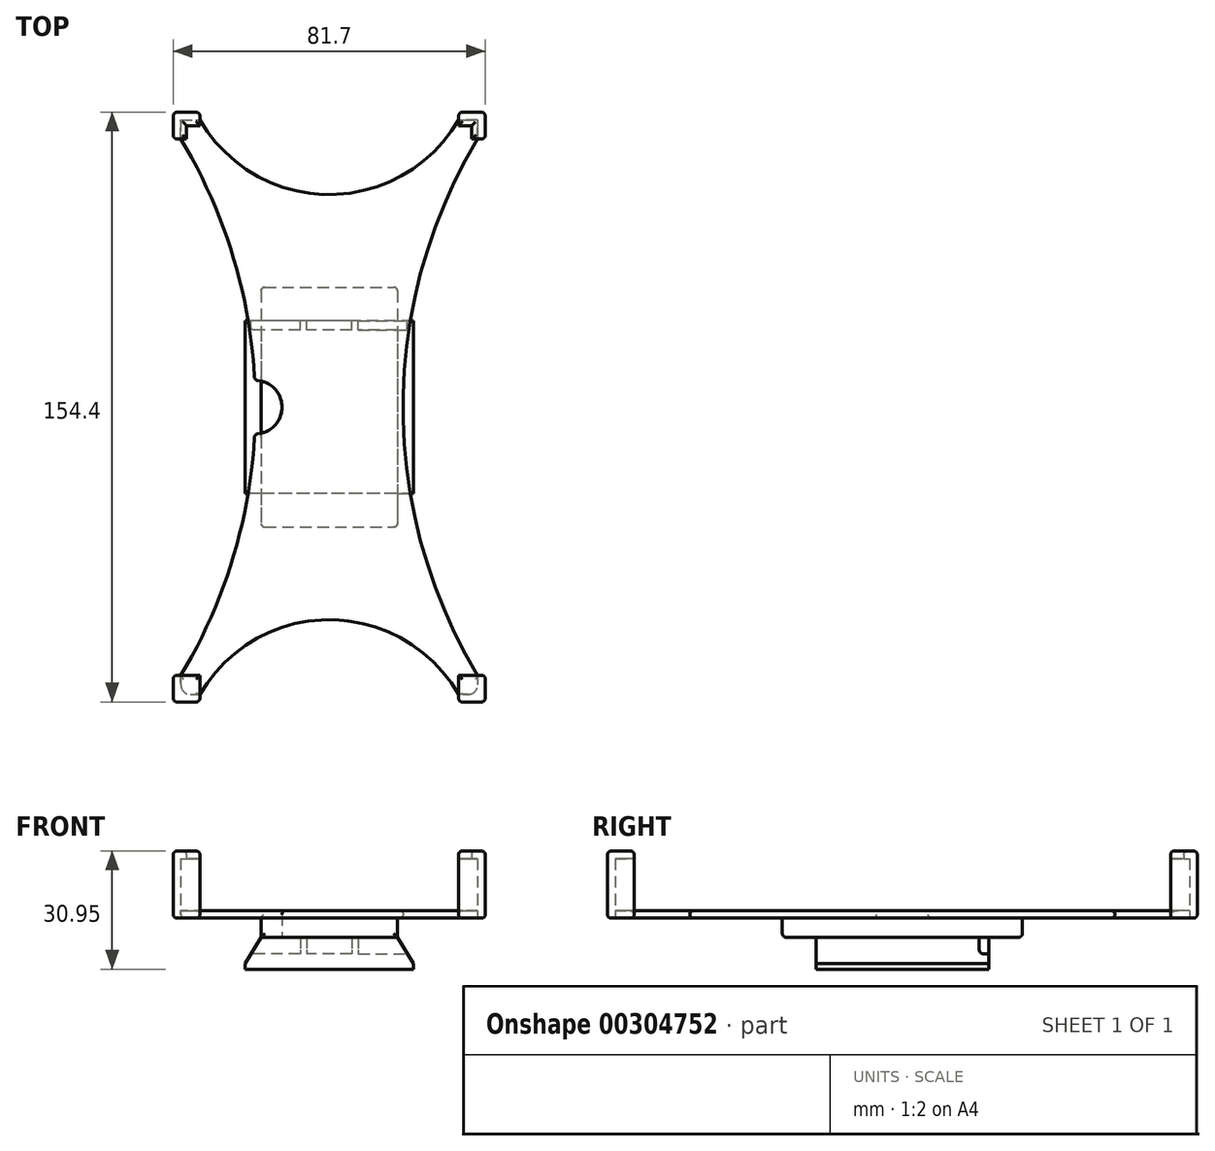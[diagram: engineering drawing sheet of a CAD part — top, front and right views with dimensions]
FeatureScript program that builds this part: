
annotation { "Feature Type Name" : "Feature", "Feature Type Description" : "" }
export const myFeature = defineFeature(function(context is Context, id is Id, definition is map)
    precondition{}
    {
        {
            var Q0;
            Q0=qCreatedBy(makeId("Top.planeOp"),FACE);
            var sketch = newSketch(context, id + "F0", { "sketchPlane" : qUnion([Q0])});
            skLineSegment(sketch, "E0.bottom", {"start": v(-38.85, 75.2) * mm, "end": v(-33.85, 75.2) * mm});
            skLineSegment(sketch, "E0.top", {"start": v(-38.85, -75.2) * mm, "end": v(-33.85, -75.2) * mm});
            skLineSegment(sketch, "E0.left", {"start": v(-38.85, 75.2) * mm, "end": v(-38.85, 70.2) * mm});
            skLineSegment(sketch, "E0.right", {"start": v(38.85, 75.2) * mm, "end": v(38.85, 70.2) * mm});
            skLineSegment(sketch, "E1", {"start": v(-38.85, 75.2) * mm, "end": v(38.85, -75.2) * mm, "construction": true});
            skArc(sketch, "E2", {"start": v(-33.85, 75.2) * mm, "mid": v(0, 55.65) * mm, "end": v(33.85, 75.2) * mm});
            skArc(sketch, "E3", {"start": v(-38.85, -70.2) * mm, "mid": v(-25.3, -39.79) * mm, "end": v(-19.53, -7) * mm});
            skArc(sketch, "E4.MirrorCS", {"start": v(38.85, -70.2) * mm, "mid": v(19.35, 0) * mm, "end": v(38.85, 70.2) * mm});
            skArc(sketch, "E5.MirrorCS", {"start": v(-33.85, -75.2) * mm, "mid": v(0, -55.65) * mm, "end": v(33.85, -75.2) * mm});
            skArc(sketch, "E6", {"start": v(-19.53, -7) * mm, "mid": v(-12.35, 0) * mm, "end": v(-19.53, 7) * mm});
            skArc(sketch, "E7.trimOffspring", {"start": v(-19.53, 7) * mm, "mid": v(-25.3, 39.79) * mm, "end": v(-38.85, 70.2) * mm});
            skLineSegment(sketch, "E8.bottom", {"start": v(-25.25, 66.5) * mm, "end": v(25.25, 66.5) * mm, "construction": true});
            skLineSegment(sketch, "E8.top", {"start": v(-25.25, 64.9) * mm, "end": v(25.25, 64.9) * mm, "construction": true});
            skLineSegment(sketch, "E8.left", {"start": v(-25.25, 66.5) * mm, "end": v(-25.25, 64.9) * mm, "construction": true});
            skLineSegment(sketch, "E8.right", {"start": v(25.25, 66.5) * mm, "end": v(25.25, 64.9) * mm, "construction": true});
            skLineSegment(sketch, "E9.trimOffspring", {"start": v(33.85, 75.2) * mm, "end": v(38.85, 75.2) * mm});
            skLineSegment(sketch, "E10.trimOffspring", {"start": v(-38.85, -70.2) * mm, "end": v(-38.85, -75.2) * mm});
            skLineSegment(sketch, "E11.trimOffspring", {"start": v(38.85, -70.2) * mm, "end": v(38.85, -75.2) * mm});
            skLineSegment(sketch, "E12.trimOffspring", {"start": v(33.85, -75.2) * mm, "end": v(38.85, -75.2) * mm});
            skSolve(sketch);
        }
        {
            var Q0;
            Q0=qSketchRegion(id+"F0",true);
            extrude(context, id + "F1", {"entities" : qUnion([Q0]), "depth" : 2 * mm});
        }
        {
            var Q0;
            Q0=qCreatedBy(makeId("Top.planeOp"),FACE);
            var sketch = newSketch(context, id + "F2", { "sketchPlane" : qUnion([Q0])});
            skLineSegment(sketch, "E13", {"start": v(-33.85, 75.2) * mm, "end": v(-33.85, 77.2) * mm});
            skLineSegment(sketch, "E14", {"start": v(-33.85, 77.2) * mm, "end": v(-40.85, 77.2) * mm});
            skLineSegment(sketch, "E15", {"start": v(-40.85, 77.2) * mm, "end": v(-40.85, 70.2) * mm});
            skLineSegment(sketch, "E16", {"start": v(-40.85, 70.2) * mm, "end": v(-38.85, 70.2) * mm});
            skLineSegment(sketch, "E17", {"start": v(-38.85, 70.2) * mm, "end": v(-38.85, 75.2) * mm});
            skLineSegment(sketch, "E18", {"start": v(-38.85, 75.2) * mm, "end": v(-33.85, 75.2) * mm});
            skLineSegment(sketch, "E19.MirrorCS", {"start": v(40.85, 77.2) * mm, "end": v(40.85, 70.2) * mm});
            skLineSegment(sketch, "E20.MirrorCS", {"start": v(33.85, 77.2) * mm, "end": v(40.85, 77.2) * mm});
            skLineSegment(sketch, "E21.MirrorCS", {"start": v(40.85, 70.2) * mm, "end": v(38.85, 70.2) * mm});
            skLineSegment(sketch, "E22.MirrorCS", {"start": v(38.85, 75.2) * mm, "end": v(33.85, 75.2) * mm});
            skLineSegment(sketch, "E23.MirrorCS", {"start": v(38.85, 70.2) * mm, "end": v(38.85, 75.2) * mm});
            skLineSegment(sketch, "E24.MirrorCS", {"start": v(33.85, 75.2) * mm, "end": v(33.85, 77.2) * mm});
            skLineSegment(sketch, "E25.MirrorCS", {"start": v(33.85, -75.2) * mm, "end": v(33.85, -77.2) * mm});
            skLineSegment(sketch, "E26.MirrorCS", {"start": v(40.85, -70.2) * mm, "end": v(38.85, -70.2) * mm});
            skLineSegment(sketch, "E27.MirrorCS", {"start": v(-33.85, -75.2) * mm, "end": v(-33.85, -77.2) * mm});
            skLineSegment(sketch, "E28.MirrorCS", {"start": v(-40.85, -70.2) * mm, "end": v(-38.85, -70.2) * mm});
            skLineSegment(sketch, "E29.MirrorCS", {"start": v(38.85, -70.2) * mm, "end": v(38.85, -75.2) * mm});
            skLineSegment(sketch, "E30.MirrorCS", {"start": v(38.85, -75.2) * mm, "end": v(33.85, -75.2) * mm});
            skLineSegment(sketch, "E31.MirrorCS", {"start": v(33.85, -77.2) * mm, "end": v(40.85, -77.2) * mm});
            skLineSegment(sketch, "E32.MirrorCS", {"start": v(40.85, -77.2) * mm, "end": v(40.85, -70.2) * mm});
            skLineSegment(sketch, "E33.MirrorCS", {"start": v(-38.85, -75.2) * mm, "end": v(-33.85, -75.2) * mm});
            skLineSegment(sketch, "E34.MirrorCS", {"start": v(-38.85, -70.2) * mm, "end": v(-38.85, -75.2) * mm});
            skLineSegment(sketch, "E35.MirrorCS", {"start": v(-33.85, -77.2) * mm, "end": v(-40.85, -77.2) * mm});
            skLineSegment(sketch, "E36.MirrorCS", {"start": v(-40.85, -77.2) * mm, "end": v(-40.85, -70.2) * mm});
            skSolve(sketch);
        }
        {
            var Q0;
            Q0=qSketchRegion(id+"F2",true);
            extrude(context, id + "F3", {"entities" : qUnion([Q0]), "operationType" : NewBodyOperationType.ADD, "depth" : (13.6 + 2) * mm});
        }
        {
            var Q0;
            Q0=makeQuery(id+"F3.opExtrude","CAP_FACE",FACE,{"disambiguationData":[OSD([sQuery(id+"F2.wireOp",EDGE,"E13"),sQuery(id+"F2.wireOp",EDGE,"E14"),sQuery(id+"F2.wireOp",EDGE,"E15"),sQuery(id+"F2.wireOp",EDGE,"E16"),sQuery(id+"F2.wireOp",EDGE,"E17"),sQuery(id+"F2.wireOp",EDGE,"E18")])],"isStart":false});
            var sketch = newSketch(context, id + "F4", { "sketchPlane" : qUnion([Q0])});
            skLineSegment(sketch, "E37.bottom", {"start": v(-40.85, -77.2) * mm, "end": v(-33.85, -77.2) * mm});
            skLineSegment(sketch, "E37.top", {"start": v(-40.85, -70.2) * mm, "end": v(-33.85, -70.2) * mm});
            skLineSegment(sketch, "E37.left", {"start": v(-40.85, -77.2) * mm, "end": v(-40.85, -70.2) * mm});
            skLineSegment(sketch, "E37.right", {"start": v(-33.85, -77.2) * mm, "end": v(-33.85, -70.2) * mm});
            skLineSegment(sketch, "E38", {"start": v(-40.85, 77.2) * mm, "end": v(-33.85, 77.2) * mm});
            skLineSegment(sketch, "E39", {"start": v(-33.85, 77.2) * mm, "end": v(-33.85, 73.7) * mm});
            skLineSegment(sketch, "E40", {"start": v(-33.85, 73.7) * mm, "end": v(-37.35, 73.7) * mm});
            skLineSegment(sketch, "E41", {"start": v(-37.35, 73.7) * mm, "end": v(-37.35, 70.2) * mm});
            skLineSegment(sketch, "E42", {"start": v(-37.35, 70.2) * mm, "end": v(-40.85, 70.2) * mm});
            skLineSegment(sketch, "E43", {"start": v(-40.85, 70.2) * mm, "end": v(-40.85, 77.2) * mm});
            skLineSegment(sketch, "E44.MirrorCS", {"start": v(33.85, 77.2) * mm, "end": v(33.85, 73.7) * mm});
            skLineSegment(sketch, "E45.MirrorCS", {"start": v(37.35, 70.2) * mm, "end": v(40.85, 70.2) * mm});
            skLineSegment(sketch, "E46.MirrorCS", {"start": v(33.85, 73.7) * mm, "end": v(37.35, 73.7) * mm});
            skLineSegment(sketch, "E47.MirrorCS", {"start": v(37.35, 73.7) * mm, "end": v(37.35, 70.2) * mm});
            skLineSegment(sketch, "E48.MirrorCS", {"start": v(40.85, -77.2) * mm, "end": v(40.85, -70.2) * mm});
            skLineSegment(sketch, "E49.MirrorCS", {"start": v(40.85, -70.2) * mm, "end": v(33.85, -70.2) * mm});
            skLineSegment(sketch, "E50.MirrorCS", {"start": v(40.85, 70.2) * mm, "end": v(40.85, 77.2) * mm});
            skLineSegment(sketch, "E51.MirrorCS", {"start": v(40.85, -77.2) * mm, "end": v(33.85, -77.2) * mm});
            skLineSegment(sketch, "E52.MirrorCS", {"start": v(40.85, 77.2) * mm, "end": v(33.85, 77.2) * mm});
            skLineSegment(sketch, "E53.MirrorCS", {"start": v(33.85, -77.2) * mm, "end": v(33.85, -70.2) * mm});
            skSolve(sketch);
        }
        {
            var Q0;
            Q0=qSketchRegion(id+"F4",true);
            extrude(context, id + "F5", {"entities" : qUnion([Q0]), "operationType" : NewBodyOperationType.ADD, "depth" : 2 * mm});
        }
        {
            var Q0;
            Q0=qCreatedBy(makeId("Top.planeOp"),FACE);
            var sketch = newSketch(context, id + "F6", { "sketchPlane" : qUnion([Q0])});
            skLineSegment(sketch, "E54.bottom", {"start": v(-17.85, 31.43) * mm, "end": v(17.85, 31.43) * mm});
            skLineSegment(sketch, "E54.top", {"start": v(-17.85, -31.42) * mm, "end": v(17.85, -31.42) * mm});
            skLineSegment(sketch, "E54.left", {"start": v(-17.85, 31.43) * mm, "end": v(-17.85, 6.84) * mm});
            skLineSegment(sketch, "E54.right", {"start": v(17.85, 31.43) * mm, "end": v(17.85, -31.42) * mm});
            skLineSegment(sketch, "E55", {"start": v(-17.85, 31.43) * mm, "end": v(17.85, -31.43) * mm, "construction": true});
            skArc(sketch, "E56", {"start": v(-17.85, -6.84) * mm, "mid": v(-12.35, 0) * mm, "end": v(-17.85, 6.84) * mm});
            skLineSegment(sketch, "E57.trimOffspring", {"start": v(-17.85, -6.84) * mm, "end": v(-17.85, -31.42) * mm});
            skSolve(sketch);
        }
        {
            var Q0;
            Q0=qSketchRegion(id+"F6",true);
            extrude(context, id + "F7", {"entities" : qUnion([Q0]), "operationType" : NewBodyOperationType.ADD, "oppositeDirection" : true, "depth" : 5 * mm});
        }
        {
            var Q0;
            Q0=makeQuery(id+"F7.opExtrude","CAP_FACE",FACE,{"disambiguationData":[OSD([sQuery(id+"F6.wireOp",EDGE,"E54.bottom"),sQuery(id+"F6.wireOp",EDGE,"E54.top"),sQuery(id+"F6.wireOp",EDGE,"E54.left"),sQuery(id+"F6.wireOp",EDGE,"E54.right"),sQuery(id+"F6.wireOp",EDGE,"E56"),sQuery(id+"F6.wireOp",EDGE,"E57.trimOffspring")])],"isStart":false});
            var sketch = newSketch(context, id + "F8", { "sketchPlane" : qUnion([Q0])});
            skLineSegment(sketch, "E58.bottom", {"start": v(17.85, -22.62) * mm, "end": v(-17.85, -22.62) * mm});
            skLineSegment(sketch, "E58.top", {"start": v(17.85, 22.62) * mm, "end": v(-17.85, 22.62) * mm});
            skLineSegment(sketch, "E58.left", {"start": v(17.85, -22.62) * mm, "end": v(17.85, 22.62) * mm});
            skLineSegment(sketch, "E58.right", {"start": v(-17.85, -22.62) * mm, "end": v(-17.85, 22.62) * mm});
            skPoint(sketch, "E58.middle", {"position": v(0, 0) * mm});
            skSolve(sketch);
        }
        {
            var Q0;
            {var subQ2=sQuery(id+"F8.wireOp",EDGE,"E58.bottom");Q0=makeQuery(id+"F8.imprint","IMPRINT",FACE,{"disambiguationData":[TD([[makeQuery(id+"F8.imprint","IMPRINT",EDGE,{"derivedFrom":subQ2}),-1.0]])]});}
            cPlane(context, id + "F9", {"entities" : qUnion([Q0]), "cplaneType" : CPlaneType.OFFSET, "offset" : 6.85 * mm, "width" : 150 * mm, "height" : 150 * mm});
        }
        {
            var Q0;
            Q0=qCreatedBy(id+"F9.planeOp",FACE);
            var sketch = newSketch(context, id + "F10", { "sketchPlane" : qUnion([Q0])});
            skLineSegment(sketch, "E59.bottom", {"start": v(22, -22.62) * mm, "end": v(-22, -22.62) * mm});
            skLineSegment(sketch, "E59.top", {"start": v(22, 22.62) * mm, "end": v(-22, 22.62) * mm});
            skLineSegment(sketch, "E59.left", {"start": v(22, -22.62) * mm, "end": v(22, 22.62) * mm});
            skLineSegment(sketch, "E59.right", {"start": v(-22, -22.62) * mm, "end": v(-22, 22.62) * mm});
            skPoint(sketch, "E59.middle", {"position": v(0, 0) * mm});
            skSolve(sketch);
        }
        {
            var Q1;
            Q1=qSketchRegion(id+"F8",true);
            var Q2;
            Q2=qSketchRegion(id+"F10",true);
            var Q3;
            Q3=sQuery(id+"F8.wireOp",VERTEX,"E58.right.end");
            var Q4;
            Q4=sQuery(id+"F10.wireOp",VERTEX,"E59.top.end");
            loft(context, id + "F11", {"operationType" : NewBodyOperationType.ADD, "sheetProfilesArray" : [{ "sheetProfileEntities" : qUnion([Q1]) }, { "sheetProfileEntities" : qUnion([Q2]) }], "matchConnections" : true, "connections" : [{ "connectionEntities" : qUnion([Q3, Q4]), "connectionEdgeQueries" : qUnion([]), "connectionEdgeParameters" : [] }]});
        }
        {
            var Q0;
            Q0=qSketchRegion(id+"F10",true);
            extrude(context, id + "F12", {"entities" : qUnion([Q0]), "operationType" : NewBodyOperationType.ADD, "depth" : 1.5 * mm});
        }
        {
            var Q0;
            Q0=makeQuery(id+"F1.opExtrude","CAP_EDGE",EDGE,{"disambiguationData":[OSD([sQuery(id+"F0.wireOp",EDGE,"E2")])],"isStart":false});
            var Q1;
            Q1=makeQuery(id+"F1.opExtrude","CAP_EDGE",EDGE,{"disambiguationData":[OSD([sQuery(id+"F0.wireOp",EDGE,"E4.MirrorCS")])],"isStart":false});
            var Q2;
            Q2=makeQuery(id+"F1.opExtrude","CAP_EDGE",EDGE,{"disambiguationData":[OSD([sQuery(id+"F0.wireOp",EDGE,"E7.trimOffspring")])],"isStart":false});
            var Q3;
            Q3=makeQuery(id+"F1.opExtrude","CAP_EDGE",EDGE,{"disambiguationData":[OSD([sQuery(id+"F0.wireOp",EDGE,"E6")])],"isStart":false});
            var Q4;
            Q4=makeQuery(id+"F1.opExtrude","CAP_EDGE",EDGE,{"disambiguationData":[OSD([sQuery(id+"F0.wireOp",EDGE,"E3")])],"isStart":false});
            var Q5;
            Q5=makeQuery(id+"F1.opExtrude","CAP_EDGE",EDGE,{"disambiguationData":[OSD([sQuery(id+"F0.wireOp",EDGE,"E5.MirrorCS")])],"isStart":false});
            var Q6;
            Q6=makeQuery(id+"F1.opExtrude","SWEPT_EDGE",EDGE,{"disambiguationData":[OSD([sQuery(id+"F0.wireOp",EDGE,"E6"),sQuery(id+"F0.wireOp",EDGE,"E7.trimOffspring")])]});
            var Q7;
            Q7=makeQuery(id+"F1.opExtrude","CAP_EDGE",EDGE,{"disambiguationData":[OSD([sQuery(id+"F0.wireOp",EDGE,"E7.trimOffspring")])],"isStart":true});
            var Q8;
            Q8=makeQuery(id+"F1.opExtrude","CAP_EDGE",EDGE,{"disambiguationData":[OSD([sQuery(id+"F0.wireOp",EDGE,"E3")])],"isStart":true});
            var Q9;
            Q9=makeQuery(id+"F1.opExtrude","SWEPT_EDGE",EDGE,{"disambiguationData":[OSD([sQuery(id+"F0.wireOp",EDGE,"E3"),sQuery(id+"F0.wireOp",EDGE,"E6")])]});
            var Q10;
            {var subQ0=sQuery(id+"F0.wireOp",EDGE,"E6");var subQ1=sQuery(id+"F0.wireOp",EDGE,"E3");Q10=makeQuery(id+"F7.boolean.opBoolean","SPLIT",EDGE,{"disambiguationData":[TD([makeQuery(id+"F1.opExtrude","SWEPT_FACE",FACE,{"disambiguationData":[OSD([subQ1])]})])],"derivedFrom":makeQuery(id+"F1.opExtrude","CAP_EDGE",EDGE,{"disambiguationData":[OSD([subQ0])],"isStart":true})});}
            var Q11;
            {var subQ0=sQuery(id+"F0.wireOp",EDGE,"E7.trimOffspring");var subQ1=sQuery(id+"F0.wireOp",EDGE,"E6");Q11=makeQuery(id+"F7.boolean.opBoolean","SPLIT",EDGE,{"disambiguationData":[TD([makeQuery(id+"F1.opExtrude","SWEPT_FACE",FACE,{"disambiguationData":[OSD([subQ0])]})])],"derivedFrom":makeQuery(id+"F1.opExtrude","CAP_EDGE",EDGE,{"disambiguationData":[OSD([subQ1])],"isStart":true})});}
            var Q12;
            Q12=makeQuery(id+"F7.opExtrude","SWEPT_EDGE",EDGE,{"disambiguationData":[OSD([sQuery(id+"F6.wireOp",EDGE,"E54.left"),sQuery(id+"F6.wireOp",EDGE,"E56")])]});
            var Q13;
            Q13=makeQuery(id+"F7.opExtrude","SWEPT_EDGE",EDGE,{"disambiguationData":[OSD([sQuery(id+"F6.wireOp",EDGE,"E56"),sQuery(id+"F6.wireOp",EDGE,"E57.trimOffspring")])]});
            var Q14;
            Q14=makeQuery(id+"F1.opExtrude","CAP_EDGE",EDGE,{"disambiguationData":[OSD([sQuery(id+"F0.wireOp",EDGE,"E2")])],"isStart":true});
            var Q15;
            Q15=makeQuery(id+"F1.opExtrude","CAP_EDGE",EDGE,{"disambiguationData":[OSD([sQuery(id+"F0.wireOp",EDGE,"E4.MirrorCS")])],"isStart":true});
            var Q16;
            Q16=makeQuery(id+"F1.opExtrude","CAP_EDGE",EDGE,{"disambiguationData":[OSD([sQuery(id+"F0.wireOp",EDGE,"E5.MirrorCS")])],"isStart":true});
            var Q17;
            Q17=makeQuery(id+"F7.opExtrude","SWEPT_EDGE",EDGE,{"disambiguationData":[OSD([sQuery(id+"F6.wireOp",EDGE,"E54.bottom"),sQuery(id+"F6.wireOp",EDGE,"E54.right")])]});
            var Q18;
            Q18=makeQuery(id+"F7.opExtrude","SWEPT_EDGE",EDGE,{"disambiguationData":[OSD([sQuery(id+"F6.wireOp",EDGE,"E54.top"),sQuery(id+"F6.wireOp",EDGE,"E54.right")])]});
            var Q19;
            Q19=makeQuery(id+"F7.opExtrude","SWEPT_EDGE",EDGE,{"disambiguationData":[OSD([sQuery(id+"F6.wireOp",EDGE,"E54.top"),sQuery(id+"F6.wireOp",EDGE,"E57.trimOffspring")])]});
            var Q20;
            Q20=makeQuery(id+"F7.opExtrude","CAP_EDGE",EDGE,{"disambiguationData":[OSD([sQuery(id+"F6.wireOp",EDGE,"E54.bottom")])],"isStart":false});
            var Q21;
            Q21=makeQuery(id+"F7.opExtrude","SWEPT_EDGE",EDGE,{"disambiguationData":[OSD([sQuery(id+"F6.wireOp",EDGE,"E54.bottom"),sQuery(id+"F6.wireOp",EDGE,"E54.left")])]});
            var Q22;
            Q22=makeQuery(id+"F7.opExtrude","CAP_EDGE",EDGE,{"disambiguationData":[OSD([sQuery(id+"F6.wireOp",EDGE,"E54.top")])],"isStart":false});
            var Q23;
            Q23=makeQuery(id+"F5.opExtrude","CAP_FACE",FACE,{"disambiguationData":[OSD([sQuery(id+"F4.wireOp",EDGE,"E48.MirrorCS"),sQuery(id+"F4.wireOp",EDGE,"E49.MirrorCS"),sQuery(id+"F4.wireOp",EDGE,"E51.MirrorCS"),sQuery(id+"F4.wireOp",EDGE,"E53.MirrorCS")])],"isStart":false});
            var Q24;
            Q24=makeQuery(id+"F5.opExtrude","CAP_FACE",FACE,{"disambiguationData":[OSD([sQuery(id+"F4.wireOp",EDGE,"E37.bottom"),sQuery(id+"F4.wireOp",EDGE,"E37.top"),sQuery(id+"F4.wireOp",EDGE,"E37.left"),sQuery(id+"F4.wireOp",EDGE,"E37.right")])],"isStart":false});
            var Q25;
            Q25=makeQuery(id+"F5.boolean.opBoolean","MERGE",EDGE,{"derivedFrom":[makeQuery(id+"F3.opExtrude","SWEPT_EDGE",EDGE,{"disambiguationData":[OSD([sQuery(id+"F2.wireOp",EDGE,"E35.MirrorCS"),sQuery(id+"F2.wireOp",EDGE,"E36.MirrorCS")])]}),makeQuery(id+"F5.opExtrude","SWEPT_EDGE",EDGE,{"disambiguationData":[OSD([sQuery(id+"F4.wireOp",EDGE,"E37.bottom"),sQuery(id+"F4.wireOp",EDGE,"E37.left")])]})]});
            var Q26;
            Q26=makeQuery(id+"F5.boolean.opBoolean","MERGE",EDGE,{"derivedFrom":[makeQuery(id+"F3.opExtrude","SWEPT_EDGE",EDGE,{"disambiguationData":[OSD([sQuery(id+"F2.wireOp",EDGE,"E31.MirrorCS"),sQuery(id+"F2.wireOp",EDGE,"E32.MirrorCS")])]}),makeQuery(id+"F5.opExtrude","SWEPT_EDGE",EDGE,{"disambiguationData":[OSD([sQuery(id+"F4.wireOp",EDGE,"E48.MirrorCS"),sQuery(id+"F4.wireOp",EDGE,"E51.MirrorCS")])]})]});
            var Q27;
            Q27=makeQuery(id+"F3.opExtrude","CAP_EDGE",EDGE,{"disambiguationData":[OSD([sQuery(id+"F2.wireOp",EDGE,"E26.MirrorCS")])],"isStart":true});
            var Q28;
            Q28=makeQuery(id+"F3.opExtrude","CAP_EDGE",EDGE,{"disambiguationData":[OSD([sQuery(id+"F2.wireOp",EDGE,"E32.MirrorCS")])],"isStart":true});
            var Q29;
            Q29=makeQuery(id+"F3.opExtrude","CAP_EDGE",EDGE,{"disambiguationData":[OSD([sQuery(id+"F2.wireOp",EDGE,"E31.MirrorCS")])],"isStart":true});
            var Q30;
            Q30=makeQuery(id+"F3.opExtrude","CAP_EDGE",EDGE,{"disambiguationData":[OSD([sQuery(id+"F2.wireOp",EDGE,"E25.MirrorCS")])],"isStart":true});
            var Q31;
            Q31=makeQuery(id+"F3.opExtrude","CAP_EDGE",EDGE,{"disambiguationData":[OSD([sQuery(id+"F2.wireOp",EDGE,"E27.MirrorCS")])],"isStart":true});
            var Q32;
            Q32=makeQuery(id+"F3.opExtrude","CAP_EDGE",EDGE,{"disambiguationData":[OSD([sQuery(id+"F2.wireOp",EDGE,"E35.MirrorCS")])],"isStart":true});
            var Q33;
            Q33=makeQuery(id+"F3.opExtrude","CAP_EDGE",EDGE,{"disambiguationData":[OSD([sQuery(id+"F2.wireOp",EDGE,"E36.MirrorCS")])],"isStart":true});
            var Q34;
            Q34=makeQuery(id+"F3.opExtrude","CAP_EDGE",EDGE,{"disambiguationData":[OSD([sQuery(id+"F2.wireOp",EDGE,"E28.MirrorCS")])],"isStart":true});
            var Q35;
            Q35=makeQuery(id+"F5.opExtrude","CAP_FACE",FACE,{"disambiguationData":[OSD([sQuery(id+"F4.wireOp",EDGE,"E38"),sQuery(id+"F4.wireOp",EDGE,"E39"),sQuery(id+"F4.wireOp",EDGE,"E40"),sQuery(id+"F4.wireOp",EDGE,"E41"),sQuery(id+"F4.wireOp",EDGE,"E42"),sQuery(id+"F4.wireOp",EDGE,"E43")])],"isStart":false});
            var Q36;
            Q36=makeQuery(id+"F5.opExtrude","CAP_FACE",FACE,{"disambiguationData":[OSD([sQuery(id+"F4.wireOp",EDGE,"E44.MirrorCS"),sQuery(id+"F4.wireOp",EDGE,"E45.MirrorCS"),sQuery(id+"F4.wireOp",EDGE,"E46.MirrorCS"),sQuery(id+"F4.wireOp",EDGE,"E47.MirrorCS"),sQuery(id+"F4.wireOp",EDGE,"E50.MirrorCS"),sQuery(id+"F4.wireOp",EDGE,"E52.MirrorCS")])],"isStart":false});
            var Q37;
            Q37=makeQuery(id+"F3.opExtrude","CAP_EDGE",EDGE,{"disambiguationData":[OSD([sQuery(id+"F2.wireOp",EDGE,"E16")])],"isStart":true});
            var Q38;
            Q38=makeQuery(id+"F3.opExtrude","CAP_EDGE",EDGE,{"disambiguationData":[OSD([sQuery(id+"F2.wireOp",EDGE,"E13")])],"isStart":true});
            var Q39;
            Q39=makeQuery(id+"F3.opExtrude","CAP_EDGE",EDGE,{"disambiguationData":[OSD([sQuery(id+"F2.wireOp",EDGE,"E14")])],"isStart":true});
            var Q40;
            Q40=makeQuery(id+"F3.opExtrude","CAP_EDGE",EDGE,{"disambiguationData":[OSD([sQuery(id+"F2.wireOp",EDGE,"E15")])],"isStart":true});
            var Q41;
            Q41=makeQuery(id+"F3.opExtrude","CAP_EDGE",EDGE,{"disambiguationData":[OSD([sQuery(id+"F2.wireOp",EDGE,"E21.MirrorCS")])],"isStart":true});
            var Q42;
            Q42=makeQuery(id+"F3.opExtrude","CAP_EDGE",EDGE,{"disambiguationData":[OSD([sQuery(id+"F2.wireOp",EDGE,"E24.MirrorCS")])],"isStart":true});
            var Q43;
            Q43=makeQuery(id+"F3.opExtrude","CAP_EDGE",EDGE,{"disambiguationData":[OSD([sQuery(id+"F2.wireOp",EDGE,"E20.MirrorCS")])],"isStart":true});
            var Q44;
            Q44=makeQuery(id+"F3.opExtrude","CAP_EDGE",EDGE,{"disambiguationData":[OSD([sQuery(id+"F2.wireOp",EDGE,"E19.MirrorCS")])],"isStart":true});
            var Q45;
            Q45=makeQuery(id+"F5.boolean.opBoolean","MERGE",EDGE,{"derivedFrom":[makeQuery(id+"F3.opExtrude","SWEPT_EDGE",EDGE,{"disambiguationData":[OSD([sQuery(id+"F2.wireOp",EDGE,"E20.MirrorCS"),sQuery(id+"F2.wireOp",EDGE,"E24.MirrorCS")])]}),makeQuery(id+"F5.opExtrude","SWEPT_EDGE",EDGE,{"disambiguationData":[OSD([sQuery(id+"F4.wireOp",EDGE,"E44.MirrorCS"),sQuery(id+"F4.wireOp",EDGE,"E52.MirrorCS")])]})]});
            var Q46;
            Q46=makeQuery(id+"F5.boolean.opBoolean","MERGE",EDGE,{"derivedFrom":[makeQuery(id+"F3.opExtrude","SWEPT_EDGE",EDGE,{"disambiguationData":[OSD([sQuery(id+"F2.wireOp",EDGE,"E19.MirrorCS"),sQuery(id+"F2.wireOp",EDGE,"E20.MirrorCS")])]}),makeQuery(id+"F5.opExtrude","SWEPT_EDGE",EDGE,{"disambiguationData":[OSD([sQuery(id+"F4.wireOp",EDGE,"E50.MirrorCS"),sQuery(id+"F4.wireOp",EDGE,"E52.MirrorCS")])]})]});
            var Q47;
            Q47=makeQuery(id+"F5.boolean.opBoolean","MERGE",EDGE,{"derivedFrom":[makeQuery(id+"F3.opExtrude","SWEPT_EDGE",EDGE,{"disambiguationData":[OSD([sQuery(id+"F2.wireOp",EDGE,"E14"),sQuery(id+"F2.wireOp",EDGE,"E15")])]}),makeQuery(id+"F5.opExtrude","SWEPT_EDGE",EDGE,{"disambiguationData":[OSD([sQuery(id+"F4.wireOp",EDGE,"E38"),sQuery(id+"F4.wireOp",EDGE,"E43")])]})]});
            var Q48;
            Q48=makeQuery(id+"F5.boolean.opBoolean","MERGE",EDGE,{"derivedFrom":[makeQuery(id+"F3.opExtrude","SWEPT_EDGE",EDGE,{"disambiguationData":[OSD([sQuery(id+"F2.wireOp",EDGE,"E15"),sQuery(id+"F2.wireOp",EDGE,"E16")])]}),makeQuery(id+"F5.opExtrude","SWEPT_EDGE",EDGE,{"disambiguationData":[OSD([sQuery(id+"F4.wireOp",EDGE,"E42"),sQuery(id+"F4.wireOp",EDGE,"E43")])]})]});
            var Q49;
            Q49=makeQuery(id+"F5.boolean.opBoolean","MERGE",EDGE,{"derivedFrom":[makeQuery(id+"F3.opExtrude","SWEPT_EDGE",EDGE,{"disambiguationData":[OSD([sQuery(id+"F2.wireOp",EDGE,"E13"),sQuery(id+"F2.wireOp",EDGE,"E14")])]}),makeQuery(id+"F5.opExtrude","SWEPT_EDGE",EDGE,{"disambiguationData":[OSD([sQuery(id+"F4.wireOp",EDGE,"E38"),sQuery(id+"F4.wireOp",EDGE,"E39")])]})]});
            var Q50;
            Q50=makeQuery(id+"F5.boolean.opBoolean","MERGE",EDGE,{"derivedFrom":[makeQuery(id+"F3.opExtrude","SWEPT_EDGE",EDGE,{"disambiguationData":[OSD([sQuery(id+"F2.wireOp",EDGE,"E19.MirrorCS"),sQuery(id+"F2.wireOp",EDGE,"E21.MirrorCS")])]}),makeQuery(id+"F5.opExtrude","SWEPT_EDGE",EDGE,{"disambiguationData":[OSD([sQuery(id+"F4.wireOp",EDGE,"E45.MirrorCS"),sQuery(id+"F4.wireOp",EDGE,"E50.MirrorCS")])]})]});
            var Q51;
            Q51=makeQuery(id+"F5.boolean.opBoolean","MERGE",EDGE,{"derivedFrom":[makeQuery(id+"F3.opExtrude","SWEPT_EDGE",EDGE,{"disambiguationData":[OSD([sQuery(id+"F2.wireOp",EDGE,"E26.MirrorCS"),sQuery(id+"F2.wireOp",EDGE,"E32.MirrorCS")])]}),makeQuery(id+"F5.opExtrude","SWEPT_EDGE",EDGE,{"disambiguationData":[OSD([sQuery(id+"F4.wireOp",EDGE,"E48.MirrorCS"),sQuery(id+"F4.wireOp",EDGE,"E49.MirrorCS")])]})]});
            var Q52;
            Q52=makeQuery(id+"F5.boolean.opBoolean","MERGE",EDGE,{"derivedFrom":[makeQuery(id+"F3.opExtrude","SWEPT_EDGE",EDGE,{"disambiguationData":[OSD([sQuery(id+"F2.wireOp",EDGE,"E25.MirrorCS"),sQuery(id+"F2.wireOp",EDGE,"E31.MirrorCS")])]}),makeQuery(id+"F5.opExtrude","SWEPT_EDGE",EDGE,{"disambiguationData":[OSD([sQuery(id+"F4.wireOp",EDGE,"E51.MirrorCS"),sQuery(id+"F4.wireOp",EDGE,"E53.MirrorCS")])]})]});
            var Q53;
            Q53=makeQuery(id+"F5.boolean.opBoolean","MERGE",EDGE,{"derivedFrom":[makeQuery(id+"F3.opExtrude","SWEPT_EDGE",EDGE,{"disambiguationData":[OSD([sQuery(id+"F2.wireOp",EDGE,"E27.MirrorCS"),sQuery(id+"F2.wireOp",EDGE,"E35.MirrorCS")])]}),makeQuery(id+"F5.opExtrude","SWEPT_EDGE",EDGE,{"disambiguationData":[OSD([sQuery(id+"F4.wireOp",EDGE,"E37.bottom"),sQuery(id+"F4.wireOp",EDGE,"E37.right")])]})]});
            var Q54;
            Q54=makeQuery(id+"F5.boolean.opBoolean","MERGE",EDGE,{"derivedFrom":[makeQuery(id+"F3.opExtrude","SWEPT_EDGE",EDGE,{"disambiguationData":[OSD([sQuery(id+"F2.wireOp",EDGE,"E28.MirrorCS"),sQuery(id+"F2.wireOp",EDGE,"E36.MirrorCS")])]}),makeQuery(id+"F5.opExtrude","SWEPT_EDGE",EDGE,{"disambiguationData":[OSD([sQuery(id+"F4.wireOp",EDGE,"E37.top"),sQuery(id+"F4.wireOp",EDGE,"E37.left")])]})]});
            fillet(context, id + "F13", {"entities" : qUnion([Q0, Q1, Q2, Q3, Q4, Q5, Q6, Q7, Q8, Q9, Q10, Q11, Q12, Q13, Q14, Q15, Q16, Q17, Q18, Q19, Q20, Q21, Q22, Q23, Q24, Q25, Q26, Q27, Q28, Q29, Q30, Q31, Q32, Q33, Q34, Q35, Q36, Q37, Q38, Q39, Q40, Q41, Q42, Q43, Q44, Q45, Q46, Q47, Q48, Q49, Q50, Q51, Q52, Q53, Q54]), "radius" : 1 * mm, "tangentPropagation" : true, "allowEdgeOverflow" : false});
        }
        {
            var Q0;
            Q0=makeQuery(id+"F1.opExtrude","CAP_EDGE",EDGE,{"disambiguationData":[OSD([sQuery(id+"F0.wireOp",EDGE,"E11.trimOffspring")])],"isStart":false});
            var Q1;
            Q1=makeQuery(id+"F1.opExtrude","CAP_EDGE",EDGE,{"disambiguationData":[OSD([sQuery(id+"F0.wireOp",EDGE,"E12.trimOffspring")])],"isStart":false});
            var Q2;
            Q2=makeQuery(id+"F3.opExtrude","SWEPT_EDGE",EDGE,{"disambiguationData":[OSD([sQuery(id+"F2.wireOp",EDGE,"E29.MirrorCS"),sQuery(id+"F2.wireOp",EDGE,"E30.MirrorCS")])]});
            var Q3;
            Q3=makeQuery(id+"F3.opExtrude","CAP_EDGE",EDGE,{"disambiguationData":[OSD([sQuery(id+"F2.wireOp",EDGE,"E30.MirrorCS")])],"isStart":false});
            var Q4;
            Q4=makeQuery(id+"F3.opExtrude","CAP_EDGE",EDGE,{"disambiguationData":[OSD([sQuery(id+"F2.wireOp",EDGE,"E29.MirrorCS")])],"isStart":false});
            var Q5;
            Q5=makeQuery(id+"F3.opExtrude","SWEPT_EDGE",EDGE,{"disambiguationData":[OSD([sQuery(id+"F2.wireOp",EDGE,"E33.MirrorCS"),sQuery(id+"F2.wireOp",EDGE,"E34.MirrorCS")])]});
            var Q6;
            Q6=makeQuery(id+"F1.opExtrude","CAP_EDGE",EDGE,{"disambiguationData":[OSD([sQuery(id+"F0.wireOp",EDGE,"E0.top")])],"isStart":false});
            var Q7;
            Q7=makeQuery(id+"F1.opExtrude","CAP_EDGE",EDGE,{"disambiguationData":[OSD([sQuery(id+"F0.wireOp",EDGE,"E10.trimOffspring")])],"isStart":false});
            var Q8;
            Q8=makeQuery(id+"F3.opExtrude","CAP_EDGE",EDGE,{"disambiguationData":[OSD([sQuery(id+"F2.wireOp",EDGE,"E33.MirrorCS")])],"isStart":false});
            var Q9;
            Q9=makeQuery(id+"F3.opExtrude","CAP_EDGE",EDGE,{"disambiguationData":[OSD([sQuery(id+"F2.wireOp",EDGE,"E34.MirrorCS")])],"isStart":false});
            var Q10;
            Q10=makeQuery(id+"F3.opExtrude","CAP_EDGE",EDGE,{"disambiguationData":[OSD([sQuery(id+"F2.wireOp",EDGE,"E17")])],"isStart":false});
            var Q11;
            Q11=makeQuery(id+"F1.opExtrude","CAP_EDGE",EDGE,{"disambiguationData":[OSD([sQuery(id+"F0.wireOp",EDGE,"E0.left")])],"isStart":false});
            var Q12;
            Q12=makeQuery(id+"F1.opExtrude","CAP_EDGE",EDGE,{"disambiguationData":[OSD([sQuery(id+"F0.wireOp",EDGE,"E0.right")])],"isStart":false});
            var Q13;
            Q13=makeQuery(id+"F3.opExtrude","CAP_EDGE",EDGE,{"disambiguationData":[OSD([sQuery(id+"F2.wireOp",EDGE,"E23.MirrorCS")])],"isStart":false});
            fillet(context, id + "F14", {"entities" : qUnion([Q0, Q1, Q2, Q3, Q4, Q5, Q6, Q7, Q8, Q9, Q10, Q11, Q12, Q13]), "radius" : 2.5 * mm, "tangentPropagation" : true, "allowEdgeOverflow" : false});
        }
        {
            var Q0;
            {var subQ0=sQuery(id+"F10.wireOp",EDGE,"E59.bottom");Q0=makeQuery(id+"F12.boolean.opBoolean","MERGE",FACE,{"derivedFrom":[makeQuery(id+"F11.opLoft","SWEPT_FACE",FACE,{"disambiguationData":[OSD([sQuery(id+"F6.wireOp",EDGE,"E54.left"),sQuery(id+"F6.wireOp",EDGE,"E54.right"),sQuery(id+"F8.wireOp",EDGE,"E58.bottom"),sQuery(id+"F8.wireOp",EDGE,"E58.left"),sQuery(id+"F8.wireOp",EDGE,"E58.right"),subQ0,sQuery(id+"F10.wireOp",EDGE,"E59.left"),sQuery(id+"F10.wireOp",EDGE,"E59.right")])]}),makeQuery(id+"F12.opExtrude","SWEPT_FACE",FACE,{"disambiguationData":[OSD([subQ0])]})]});}
            var sketch = newSketch(context, id + "F15", { "sketchPlane" : qUnion([Q0])});
            skLineSegment(sketch, "E60", {"start": v(0, -5) * mm, "end": v(-5.9, -5) * mm});
            skLineSegment(sketch, "E61", {"start": v(-5.9, -5) * mm, "end": v(-5.9, -9.3) * mm});
            skLineSegment(sketch, "E62", {"start": v(-5.9, -9.3) * mm, "end": v(0, -9.3) * mm});
            skLineSegment(sketch, "E63", {"start": v(-17.85, -5) * mm, "end": v(-7.6, -5) * mm});
            skLineSegment(sketch, "E64", {"start": v(-7.6, -5) * mm, "end": v(-7.6, -9.3) * mm});
            skLineSegment(sketch, "E65", {"start": v(-7.6, -9.3) * mm, "end": v(-20.46, -9.3) * mm});
            skLineSegment(sketch, "E66", {"start": v(-20.46, -9.3) * mm, "end": v(-17.85, -5) * mm});
            skLineSegment(sketch, "E67.MirrorCS", {"start": v(7.6, -5) * mm, "end": v(7.6, -9.3) * mm});
            skLineSegment(sketch, "E68.MirrorCS", {"start": v(17.85, -5) * mm, "end": v(7.6, -5) * mm});
            skLineSegment(sketch, "E69.MirrorCS", {"start": v(20.46, -9.3) * mm, "end": v(17.85, -5) * mm});
            skLineSegment(sketch, "E70.MirrorCS", {"start": v(5.9, -9.3) * mm, "end": v(0, -9.3) * mm});
            skLineSegment(sketch, "E71.MirrorCS", {"start": v(5.9, -5) * mm, "end": v(5.9, -9.3) * mm});
            skLineSegment(sketch, "E72.MirrorCS", {"start": v(0, -5) * mm, "end": v(5.9, -5) * mm});
            skLineSegment(sketch, "E73.MirrorCS", {"start": v(7.6, -9.3) * mm, "end": v(20.46, -9.3) * mm});
            skSolve(sketch);
        }
        {
            var Q0;
            Q0=qSketchRegion(id+"F15",true);
            extrude(context, id + "F16", {"entities" : qUnion([Q0]), "operationType" : NewBodyOperationType.REMOVE, "oppositeDirection" : true, "depth" : 2.5 * mm});
        }
        {
            var Q0;
            Q0=makeQuery(id+"F16.boolean.opBoolean","COPY",EDGE,{"derivedFrom":makeQuery(id+"F16.opExtrude","CAP_EDGE",EDGE,{"disambiguationData":[OSD([sQuery(id+"F15.wireOp",EDGE,"E65")])],"isStart":false})});
            var Q1;
            Q1=makeQuery(id+"F16.boolean.opBoolean","COPY",EDGE,{"derivedFrom":makeQuery(id+"F16.opExtrude","CAP_EDGE",EDGE,{"disambiguationData":[OSD([sQuery(id+"F15.wireOp",EDGE,"E62"),sQuery(id+"F15.wireOp",EDGE,"E70.MirrorCS")])],"isStart":false})});
            var Q2;
            Q2=makeQuery(id+"F16.boolean.opBoolean","COPY",EDGE,{"derivedFrom":makeQuery(id+"F16.opExtrude","CAP_EDGE",EDGE,{"disambiguationData":[OSD([sQuery(id+"F15.wireOp",EDGE,"E73.MirrorCS")])],"isStart":false})});
            fillet(context, id + "F17", {"entities" : qUnion([Q0, Q1, Q2]), "radius" : 1 * mm, "tangentPropagation" : true, "allowEdgeOverflow" : false});
        }
    });
